# Revit family: QF_ADVENTYS_ADV1886-B_KTI2_325x600_10000_W_Géné_déporté
name_source: partatom
category: Attrezzature speciali
units: mm (PartAtom-declared; Revit-internal decimal feet)

## family parameters
Condiviso = No
Host = Superficie
Punto di calcolo locali = No
Quota connettore circolare = Usa diametro
Taglio con vuoti quando caricato = No
Tipo di parte = Normale

## types (1)
- ADV1886-B
    Controller_Height = 120 mm  [stored 0.393701 ft]
    Controller_Width = 394 mm
    Cycle = 50 Hz
    Depth = 600 mm
    Depth Actual = 600 mm
    Height = 63 mm  [stored 0.206693 ft]
    Height Actual = 63 mm  [stored 0.206693 ft]
    Item Number = ADV1886-B
    Length Actual = 325 mm  [stored 1.06627 ft]
    Modello = KTI2 325x600 10000 W Géné déporté
    Phase = 3
    Produttore = ADVENTYS
    Prospetto di default = 1219.2 mm  [stored 4 ft]
    URL = https://adventys.com
    Volts = 380 V
    Watts = 10000 W
    Weight = 30
    Width = 325 mm  [stored 1.06627 ft]

note: [stored X ft] marks values corroborated as IEEE doubles in the binary element streams (Revit-internal decimal feet)

## geometry (parser evidence)
native form markers: Sweep x1
no freeform markers — native parametric forms only
